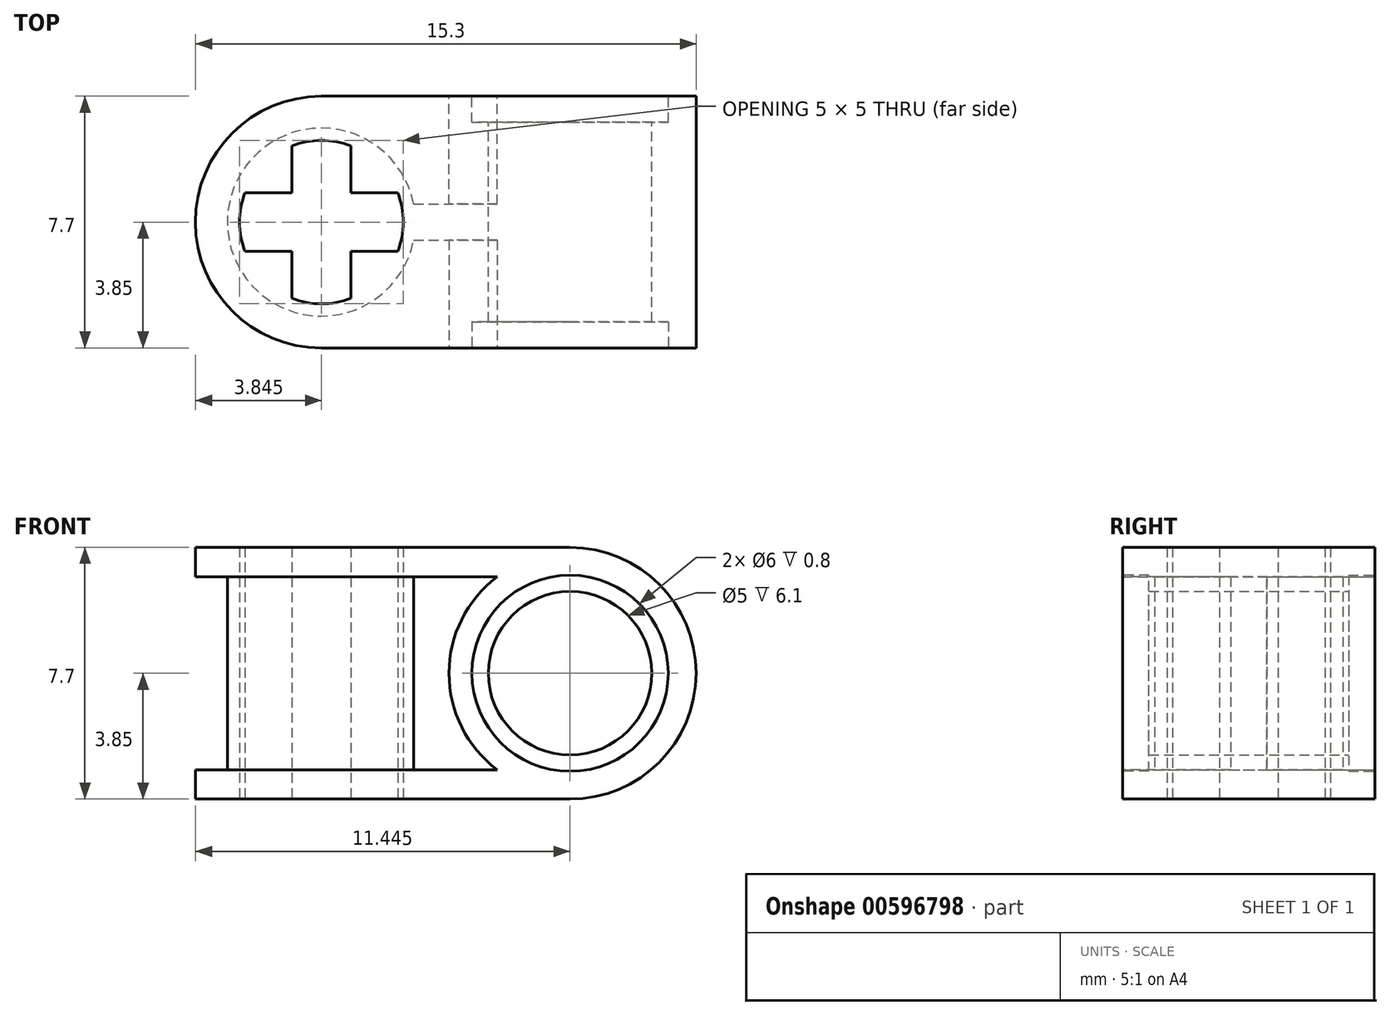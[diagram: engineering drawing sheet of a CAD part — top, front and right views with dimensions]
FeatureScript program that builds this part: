
annotation { "Feature Type Name" : "Feature", "Feature Type Description" : "" }
export const myFeature = defineFeature(function(context is Context, id is Id, definition is map)
    precondition{}
    {
        {
            var Q0;
            Q0=qCreatedBy(makeId("Front.planeOp"),FACE);
            var sketch = newSketch(context, id + "F0", { "sketchPlane" : qUnion([Q0])});
            skLineSegment(sketch, "E0.bottom", {"start": v(-19.56, 7.3) * mm, "end": v(-4.26, 7.3) * mm});
            skLineSegment(sketch, "E0.top", {"start": v(-19.56, -0.4) * mm, "end": v(-4.26, -0.4) * mm});
            skLineSegment(sketch, "E0.left", {"start": v(-19.56, 7.3) * mm, "end": v(-19.56, -0.4) * mm});
            skLineSegment(sketch, "E0.right", {"start": v(-4.26, 7.3) * mm, "end": v(-4.26, -0.4) * mm});
            skSolve(sketch);
        }
        {
            var Q0;
            Q0=qCreatedBy(makeId("Front.planeOp"),FACE);
            var sketch = newSketch(context, id + "F1", { "sketchPlane" : qUnion([Q0])});
            skSolve(sketch);
        }
        {
            var Q0;
            Q0=qSketchRegion(id+"F1",true);
            var Q1;
            Q1=makeQuery(id+"F0.imprint","IMPRINT",FACE,{"disambiguationData":[TD([[makeQuery(id+"F0.imprint","IMPRINT",EDGE,{"derivedFrom":sQuery(id+"F0.wireOp",EDGE,"E0.bottom")}),-1.0]])]});
            extrude(context, id + "F2", {"entities" : qUnion([Q0, Q1]), "depth" : 7.7 * mm});
        }
        {
            var Q0;
            Q0=makeQuery(id+"F2.opExtrude","CAP_EDGE",EDGE,{"disambiguationData":[OSD([sQuery(id+"F0.wireOp",EDGE,"E0.left")])],"isStart":true});
            var Q1;
            Q1=makeQuery(id+"F2.opExtrude","CAP_EDGE",EDGE,{"disambiguationData":[OSD([sQuery(id+"F0.wireOp",EDGE,"E0.left")])],"isStart":false});
            var Q2;
            Q2=makeQuery(id+"F2.opExtrude","SWEPT_EDGE",EDGE,{"disambiguationData":[OSD([sQuery(id+"F0.wireOp",EDGE,"E0.bottom"),sQuery(id+"F0.wireOp",EDGE,"E0.right")])]});
            var Q3;
            Q3=makeQuery(id+"F2.opExtrude","SWEPT_EDGE",EDGE,{"disambiguationData":[OSD([sQuery(id+"F0.wireOp",EDGE,"E0.top"),sQuery(id+"F0.wireOp",EDGE,"E0.right")])]});
            fillet(context, id + "F3", {"entities" : qUnion([Q0, Q1, Q2, Q3]), "radius" : 3.85 * mm, "tangentPropagation" : true, "allowEdgeOverflow" : false});
        }
        {
            var Q0;
            Q0=makeQuery(id+"F2.opExtrude","CAP_FACE",FACE,{"disambiguationData":[OSD([sQuery(id+"F0.wireOp",EDGE,"E0.bottom"),sQuery(id+"F0.wireOp",EDGE,"E0.top"),sQuery(id+"F0.wireOp",EDGE,"E0.left"),sQuery(id+"F0.wireOp",EDGE,"E0.right")])],"isStart":true});
            var sketch = newSketch(context, id + "F4", { "sketchPlane" : qUnion([Q0])});
            skLineSegment(sketch, "E1", {"start": v(4.26, 3.45) * mm, "end": v(30.5, 3.45) * mm, "construction": true});
            skCircle(sketch, "E2", {"center": v(8.11, 3.45) * mm, "radius": 2.5 * mm});
            skSolve(sketch);
        }
        {
            var Q0;
            Q0=makeQuery(id+"F4.imprint","IMPRINT",FACE,{"disambiguationData":[TD([[makeQuery(id+"F4.imprint","IMPRINT",EDGE,{"derivedFrom":sQuery(id+"F4.wireOp",EDGE,"E2")}),1.0]])]});
            extrude(context, id + "F5", {"entities" : qUnion([Q0]), "operationType" : NewBodyOperationType.REMOVE, "oppositeDirection" : true, "depth" : 59 * mm});
        }
        {
            var Q0;
            Q0=makeQuery(id+"F2.opExtrude","CAP_FACE",FACE,{"disambiguationData":[OSD([sQuery(id+"F0.wireOp",EDGE,"E0.bottom"),sQuery(id+"F0.wireOp",EDGE,"E0.top"),sQuery(id+"F0.wireOp",EDGE,"E0.left"),sQuery(id+"F0.wireOp",EDGE,"E0.right")])],"isStart":true});
            var sketch = newSketch(context, id + "F6", { "sketchPlane" : qUnion([Q0])});
            skLineSegment(sketch, "E3", {"start": v(4.26, 3.45) * mm, "end": v(33.97, 3.45) * mm, "construction": true});
            skCircle(sketch, "E4", {"center": v(8.11, 3.45) * mm, "radius": 3 * mm});
            skSolve(sketch);
        }
        {
            var Q0;
            Q0=makeQuery(id+"F6.imprint","IMPRINT",FACE,{"disambiguationData":[TD([[makeQuery(id+"F6.imprint","IMPRINT",EDGE,{"derivedFrom":makeQuery(id+"F5.boolean.opBoolean","COPY",EDGE,{"derivedFrom":makeQuery(id+"F5.opExtrude","CAP_EDGE",EDGE,{"disambiguationData":[OSD([sQuery(id+"F4.wireOp",EDGE,"E2")])],"isStart":true})})}),1.0]])]});
            var Q1;
            Q1=makeQuery(id+"F6.imprint","IMPRINT",FACE,{"disambiguationData":[TD([[makeQuery(id+"F6.imprint","IMPRINT",EDGE,{"derivedFrom":sQuery(id+"F6.wireOp",EDGE,"E4")}),1.0]])]});
            extrude(context, id + "F7", {"entities" : qUnion([Q0, Q1]), "operationType" : NewBodyOperationType.REMOVE, "oppositeDirection" : true, "depth" : 0.8 * mm});
        }
        {
            var Q0;
            Q0=makeQuery(id+"F2.opExtrude","CAP_FACE",FACE,{"disambiguationData":[OSD([sQuery(id+"F0.wireOp",EDGE,"E0.bottom"),sQuery(id+"F0.wireOp",EDGE,"E0.top"),sQuery(id+"F0.wireOp",EDGE,"E0.left"),sQuery(id+"F0.wireOp",EDGE,"E0.right")])],"isStart":false});
            var sketch = newSketch(context, id + "F8", { "sketchPlane" : qUnion([Q0])});
            skLineSegment(sketch, "E5", {"start": v(-4.26, 3.45) * mm, "end": v(-37.9, 3.45) * mm, "construction": true});
            skPoint(sketch, "E5.endSnap0", {"position": v(-15.71, 3.45) * mm});
            skCircle(sketch, "E6", {"center": v(-8.11, 3.45) * mm, "radius": 3 * mm});
            skSolve(sketch);
        }
        {
            var Q0;
            Q0=makeQuery(id+"F8.imprint","IMPRINT",FACE,{"disambiguationData":[TD([[makeQuery(id+"F8.imprint","IMPRINT",EDGE,{"derivedFrom":makeQuery(id+"F5.boolean.opBoolean","INTERSECT",EDGE,{"derivedFrom":[makeQuery(id+"F2.opExtrude","CAP_FACE",FACE,{"disambiguationData":[OSD([sQuery(id+"F0.wireOp",EDGE,"E0.bottom"),sQuery(id+"F0.wireOp",EDGE,"E0.top"),sQuery(id+"F0.wireOp",EDGE,"E0.left"),sQuery(id+"F0.wireOp",EDGE,"E0.right")])],"isStart":false}),makeQuery(id+"F5.opExtrude","SWEPT_FACE",FACE,{"disambiguationData":[OSD([sQuery(id+"F4.wireOp",EDGE,"E2")])]})]})}),1.0]])]});
            var Q1;
            Q1=makeQuery(id+"F8.imprint","IMPRINT",FACE,{"disambiguationData":[TD([[makeQuery(id+"F8.imprint","IMPRINT",EDGE,{"derivedFrom":sQuery(id+"F8.wireOp",EDGE,"E6")}),1.0]])]});
            extrude(context, id + "F9", {"entities" : qUnion([Q0, Q1]), "operationType" : NewBodyOperationType.REMOVE, "oppositeDirection" : true, "depth" : 0.8 * mm});
        }
        {
            var Q0;
            Q0=makeQuery(id+"F2.opExtrude","CAP_FACE",FACE,{"disambiguationData":[OSD([sQuery(id+"F0.wireOp",EDGE,"E0.bottom"),sQuery(id+"F0.wireOp",EDGE,"E0.top"),sQuery(id+"F0.wireOp",EDGE,"E0.left"),sQuery(id+"F0.wireOp",EDGE,"E0.right")])],"isStart":false});
            var sketch = newSketch(context, id + "F10", { "sketchPlane" : qUnion([Q0])});
            skCircle(sketch, "E7", {"center": v(-8.11, 3.45) * mm, "radius": 3.7 * mm});
            skLineSegment(sketch, "E8", {"start": v(-15.71, 7.3) * mm, "end": v(-15.71, 6.4) * mm, "construction": true});
            skLineSegment(sketch, "E9", {"start": v(-15.71, 6.4) * mm, "end": v(-10.35, 6.4) * mm});
            skLineSegment(sketch, "E10", {"start": v(-15.71, -0.4) * mm, "end": v(-15.71, 0.5) * mm, "construction": true});
            skLineSegment(sketch, "E11", {"start": v(-15.71, 0.5) * mm, "end": v(-10.35, 0.5) * mm});
            skSolve(sketch);
        }
        {
            var Q0;
            {var subQ0=sQuery(id+"F10.wireOp",EDGE,"E9");Q0=makeQuery(id+"F10.imprint","IMPRINT",FACE,{"disambiguationData":[TD([[makeQuery(id+"F10.imprint","IMPRINT",EDGE,{"derivedFrom":subQ0}),-1.0]])]});}
            extrude(context, id + "F11", {"entities" : qUnion([Q0]), "operationType" : NewBodyOperationType.REMOVE, "oppositeDirection" : true, "depth" : 3.3 * mm});
        }
        {
            var Q0;
            Q0=makeQuery(id+"F2.opExtrude","CAP_FACE",FACE,{"disambiguationData":[OSD([sQuery(id+"F0.wireOp",EDGE,"E0.bottom"),sQuery(id+"F0.wireOp",EDGE,"E0.top"),sQuery(id+"F0.wireOp",EDGE,"E0.left"),sQuery(id+"F0.wireOp",EDGE,"E0.right")])],"isStart":true});
            var sketch = newSketch(context, id + "F12", { "sketchPlane" : qUnion([Q0])});
            skLineSegment(sketch, "E12", {"start": v(15.71, 7.3) * mm, "end": v(15.71, 6.4) * mm, "construction": true});
            skCircle(sketch, "E13", {"center": v(8.11, 3.45) * mm, "radius": 3.7 * mm});
            skLineSegment(sketch, "E14", {"start": v(15.71, 6.4) * mm, "end": v(10.35, 6.4) * mm});
            skLineSegment(sketch, "E15", {"start": v(15.71, -0.4) * mm, "end": v(15.71, 0.5) * mm, "construction": true});
            skLineSegment(sketch, "E16", {"start": v(15.71, 0.5) * mm, "end": v(10.35, 0.5) * mm});
            skSolve(sketch);
        }
        {
            var Q0;
            {var subQ0=sQuery(id+"F12.wireOp",EDGE,"E14");Q0=makeQuery(id+"F12.imprint","IMPRINT",FACE,{"disambiguationData":[TD([[makeQuery(id+"F12.imprint","IMPRINT",EDGE,{"derivedFrom":subQ0}),1.0]])]});}
            extrude(context, id + "F13", {"entities" : qUnion([Q0]), "operationType" : NewBodyOperationType.REMOVE, "oppositeDirection" : true, "depth" : 3.3 * mm});
        }
        {
            var Q0;
            Q0=makeQuery(id+"F2.opExtrude","SWEPT_FACE",FACE,{"disambiguationData":[OSD([sQuery(id+"F0.wireOp",EDGE,"E0.top")])]});
            var sketch = newSketch(context, id + "F14", { "sketchPlane" : qUnion([Q0])});
            skCircle(sketch, "E17", {"center": v(-15.71, 3.85) * mm, "radius": 2.5 * mm});
            skPoint(sketch, "E18.endSnap0", {"position": v(-19.56, 3.85) * mm});
            skLineSegment(sketch, "E19", {"start": v(-14.81, 4.75) * mm, "end": v(-14.81, 6.18) * mm});
            skLineSegment(sketch, "E20", {"start": v(-14.81, 4.75) * mm, "end": v(-13.38, 4.75) * mm});
            skLineSegment(sketch, "E21", {"start": v(-14.81, 2.95) * mm, "end": v(-13.38, 2.95) * mm});
            skLineSegment(sketch, "E22", {"start": v(-14.81, 2.95) * mm, "end": v(-14.81, 1.52) * mm});
            skLineSegment(sketch, "E23", {"start": v(-16.61, 2.95) * mm, "end": v(-16.61, 1.52) * mm});
            skLineSegment(sketch, "E24", {"start": v(-16.61, 4.75) * mm, "end": v(-18.05, 4.75) * mm});
            skLineSegment(sketch, "E25", {"start": v(-16.61, 2.95) * mm, "end": v(-18.05, 2.95) * mm});
            skLineSegment(sketch, "E26", {"start": v(-16.61, 4.75) * mm, "end": v(-16.61, 6.18) * mm});
            skLineSegment(sketch, "E27", {"start": v(-18.21, 3.85) * mm, "end": v(-18.21, -2.5) * mm, "construction": true});
            skLineSegment(sketch, "E28", {"start": v(-16.61, 4.75) * mm, "end": v(-16.61, 2.95) * mm, "construction": true});
            skCircle(sketch, "E29", {"center": v(-15.71, 3.85) * mm, "radius": 2.88 * mm});
            skLineSegment(sketch, "E30", {"start": v(-15.71, 7.7) * mm, "end": v(-15.71, 6.72) * mm});
            skLineSegment(sketch, "E31", {"start": v(-15.71, 0) * mm, "end": v(-15.71, 0.98) * mm});
            skSolve(sketch);
        }
        {
            var Q0;
            {var subQ4=sQuery(id+"F14.wireOp",EDGE,"E19");Q0=makeQuery(id+"F14.imprint","IMPRINT",FACE,{"disambiguationData":[TD([[makeQuery(id+"F14.imprint","IMPRINT",EDGE,{"derivedFrom":subQ4}),1.0]])]});}
            extrude(context, id + "F15", {"entities" : qUnion([Q0]), "operationType" : NewBodyOperationType.REMOVE, "oppositeDirection" : true, "depth" : 10 * mm});
        }
        {
            var Q0;
            Q0=qSketchRegion(id+"F14",true);
            var Q1;
            Q1=makeQuery(id+"F2.opExtrude","SWEPT_FACE",FACE,{"disambiguationData":[OSD([sQuery(id+"F0.wireOp",EDGE,"E0.bottom")])]});
            extrude(context, id + "F16", {"entities" : qUnion([Q0]), "operationType" : NewBodyOperationType.ADD, "endBound" : BoundingType.UP_TO_SURFACE, "oppositeDirection" : true, "endBoundEntityFace" : qUnion([Q1]), "depth" : 25 * mm});
        }
        {
            var Q0;
            {var subQ0=sQuery(id+"F14.wireOp",EDGE,"E23");Q0=makeQuery(id+"F14.imprint","IMPRINT",FACE,{"disambiguationData":[TD([[makeQuery(id+"F14.imprint","IMPRINT",EDGE,{"derivedFrom":subQ0}),-1.0]])]});}
            var Q1;
            {var subQ0=sQuery(id+"F14.wireOp",EDGE,"E19");Q1=makeQuery(id+"F14.imprint","IMPRINT",FACE,{"disambiguationData":[TD([[makeQuery(id+"F14.imprint","IMPRINT",EDGE,{"derivedFrom":subQ0}),-1.0]])]});}
            var Q2;
            {var subQ0=sQuery(id+"F14.wireOp",EDGE,"E21");Q2=makeQuery(id+"F14.imprint","IMPRINT",FACE,{"disambiguationData":[TD([[makeQuery(id+"F14.imprint","IMPRINT",EDGE,{"derivedFrom":subQ0}),-1.0]])]});}
            var Q3;
            {var subQ0=sQuery(id+"F14.wireOp",EDGE,"E24");Q3=makeQuery(id+"F14.imprint","IMPRINT",FACE,{"disambiguationData":[TD([[makeQuery(id+"F14.imprint","IMPRINT",EDGE,{"derivedFrom":subQ0}),-1.0]])]});}
            var Q4;
            Q4=makeQuery(id+"F2.opExtrude","SWEPT_FACE",FACE,{"disambiguationData":[OSD([sQuery(id+"F0.wireOp",EDGE,"E0.bottom")])]});
            extrude(context, id + "F17", {"entities" : qUnion([Q0, Q1, Q2, Q3]), "operationType" : NewBodyOperationType.ADD, "endBound" : BoundingType.UP_TO_SURFACE, "oppositeDirection" : true, "endBoundEntityFace" : qUnion([Q4]), "depth" : 25 * mm});
        }
        {
            var Q0;
            {var subQ0=sQuery(id+"F14.wireOp",EDGE,"E30");Q0=makeQuery(id+"F14.imprint","IMPRINT",FACE,{"disambiguationData":[TD([[makeQuery(id+"F14.imprint","IMPRINT",EDGE,{"derivedFrom":subQ0}),-1.0]])]});}
            var Q1;
            {var subQ0=sQuery(id+"F10.wireOp",EDGE,"E9");var subQ3=sQuery(id+"F0.wireOp",EDGE,"E0.left");Q1=makeQuery(id+"F16.boolean.opBoolean","SPLIT",FACE,{"disambiguationData":[TD([makeQuery(id+"F3.opFillet","BLEND_FACE",FACE,{"disambiguationData":[OSD([subQ3])]})])],"derivedFrom":makeQuery(id+"F11.boolean.opBoolean","COPY",FACE,{"derivedFrom":makeQuery(id+"F11.opExtrude","SWEPT_FACE",FACE,{"disambiguationData":[OSD([subQ0])]})})});}
            extrude(context, id + "F18", {"entities" : qUnion([Q0]), "operationType" : NewBodyOperationType.REMOVE, "endBound" : BoundingType.UP_TO_SURFACE, "oppositeDirection" : true, "endBoundEntityFace" : qUnion([Q1]), "depth" : 25 * mm});
        }
        {
            var Q0;
            {var subQ0=sQuery(id+"F14.wireOp",EDGE,"E30");Q0=makeQuery(id+"F14.imprint","IMPRINT",FACE,{"disambiguationData":[TD([[makeQuery(id+"F14.imprint","IMPRINT",EDGE,{"derivedFrom":subQ0}),-1.0]])]});}
            var Q1;
            {var subQ0=sQuery(id+"F10.wireOp",EDGE,"E11");var subQ3=sQuery(id+"F0.wireOp",EDGE,"E0.left");Q1=makeQuery(id+"F16.boolean.opBoolean","SPLIT",FACE,{"disambiguationData":[TD([makeQuery(id+"F3.opFillet","BLEND_FACE",FACE,{"disambiguationData":[OSD([subQ3])]})])],"derivedFrom":makeQuery(id+"F11.boolean.opBoolean","COPY",FACE,{"derivedFrom":makeQuery(id+"F11.opExtrude","SWEPT_FACE",FACE,{"disambiguationData":[OSD([subQ0])]})})});}
            extrude(context, id + "F19", {"entities" : qUnion([Q0]), "operationType" : NewBodyOperationType.ADD, "endBound" : BoundingType.UP_TO_SURFACE, "oppositeDirection" : true, "endBoundEntityFace" : qUnion([Q1]), "depth" : 25 * mm});
        }
    });
